# Revit family: Bisley_Essentials_Tambour_800mm_Wide
name_source: partatom
category: Furniture
revit_build: Autodesk Revit 2018 (Build: 20170223_1515(x64)
units: mm (PartAtom-declared; Revit-internal decimal feet)

## family parameters
Always vertical = No
Cut with Voids When Loaded = No
OmniClass Number = 23.40.20.00
OmniClass Title = General Furniture and Specialties
Room Calculation Point = No
Shared = No
Work Plane-Based = No

## types (12) — shared parameters
Bisely_Width = 800 mm
Bisley_Depth = 470 mm
Category = Furniture
Manufacturer = Bisley
ManufacturerName = Bisley
URL = www.bisley.com
Uniclass2015Code = Pr_40_30_78
Uniclass2015Title = Shelves and storage units
Uniclass2015Version = v1.5
WarrantyDurationUnit = 5 Years

## per-type parameters (varying)
| type | Assembly Code | Bisley_Height | Bisley_Tambour_Material | Description | Model | Type Comments |
| YETB0812/2S |  | 1270 mm | <By Category> | Essentials 800mm wide Tambour including 2 shelves | YETB0812/2S | Height is adjustable up to 24mm (1”) in total |
| YETB0819 |  | 1970 mm | <By Category> | Essentials 800mm wide Tambour, empty | YETB0819 | Height is adjustable up to 24mm (1”) in total |
| YETB0815/3S |  | 1570 mm | <By Category> | Essentials 800mm wide Tambour including 3 shelves | YETB0815/3S | Height is adjustable up to 24mm (1”) in total |
| YETB0815 |  | 1570 mm | <By Category> | Essentials 800mm wide Tambour, empty | YETB0815 | Height is adjustable up to 24mm (1”) in total |
| YETB0811 |  | 1070 mm | <By Category> | Essentials 800mm wide Tambour, empty | YETB0811 | Height is adjustable up to 24mm (1”) in total |
| YETB0810/1S |  | 1000 mm  [stored 3.28084 ft] | <By Category> | Essentials 800mm wide Tambour including 1 shelf | YETB0810/1S | Height is adjustable up to 24mm (1”) in total |
| YETB0810 |  | 1000 mm  [stored 3.28084 ft] | <By Category> | Essentials 800mm wide Tambour, empty
Essentials 800mm wide Tambour, empty | YETB0810 | Height is adjustable up to 24mm (1”) in total |
| YETBDH0807/1S |  | 718 mm | <By Category> | Essentials Desk High 800mm wide Tambour including 1 shelf | YETBDH0807/1S | Height is adjustable up to 8mm (0.3”) in total |
| YETB0807/1S | Essentials 800mm wide Tambour including 1 shelf | 693 mm  [stored 2.27362 ft] | Bisley - ARN - Silver | Steel Tambour + 1 Shelf | YETB0807/1S | Height is adjustable up to 8mm (0.3”) in total |
| YETB0819/4S |  | 1970 mm | <By Category> | Essentials 800mm wide Tambour including 4 shelves | YETB0819/4S | Height is adjustable up to 24mm (1”) in total |
| YETB0811/1S |  | 1070 mm | <By Category> | Essentials 800mm wide Tambour including 1 shelf | YETB0811/S | Height is adjustable up to 24mm (1”) in total |
| YETB0812 |  | 1270 mm | <By Category> | Essentials 800mm wide Tambour, empty | YETB0812 | Height is adjustable up to 24mm (1”) in total |

note: [stored X ft] marks values corroborated as IEEE doubles in the binary element streams (Revit-internal decimal feet)

## geometry (parser evidence)
native form markers: Sweep x4
no freeform markers — native parametric forms only
